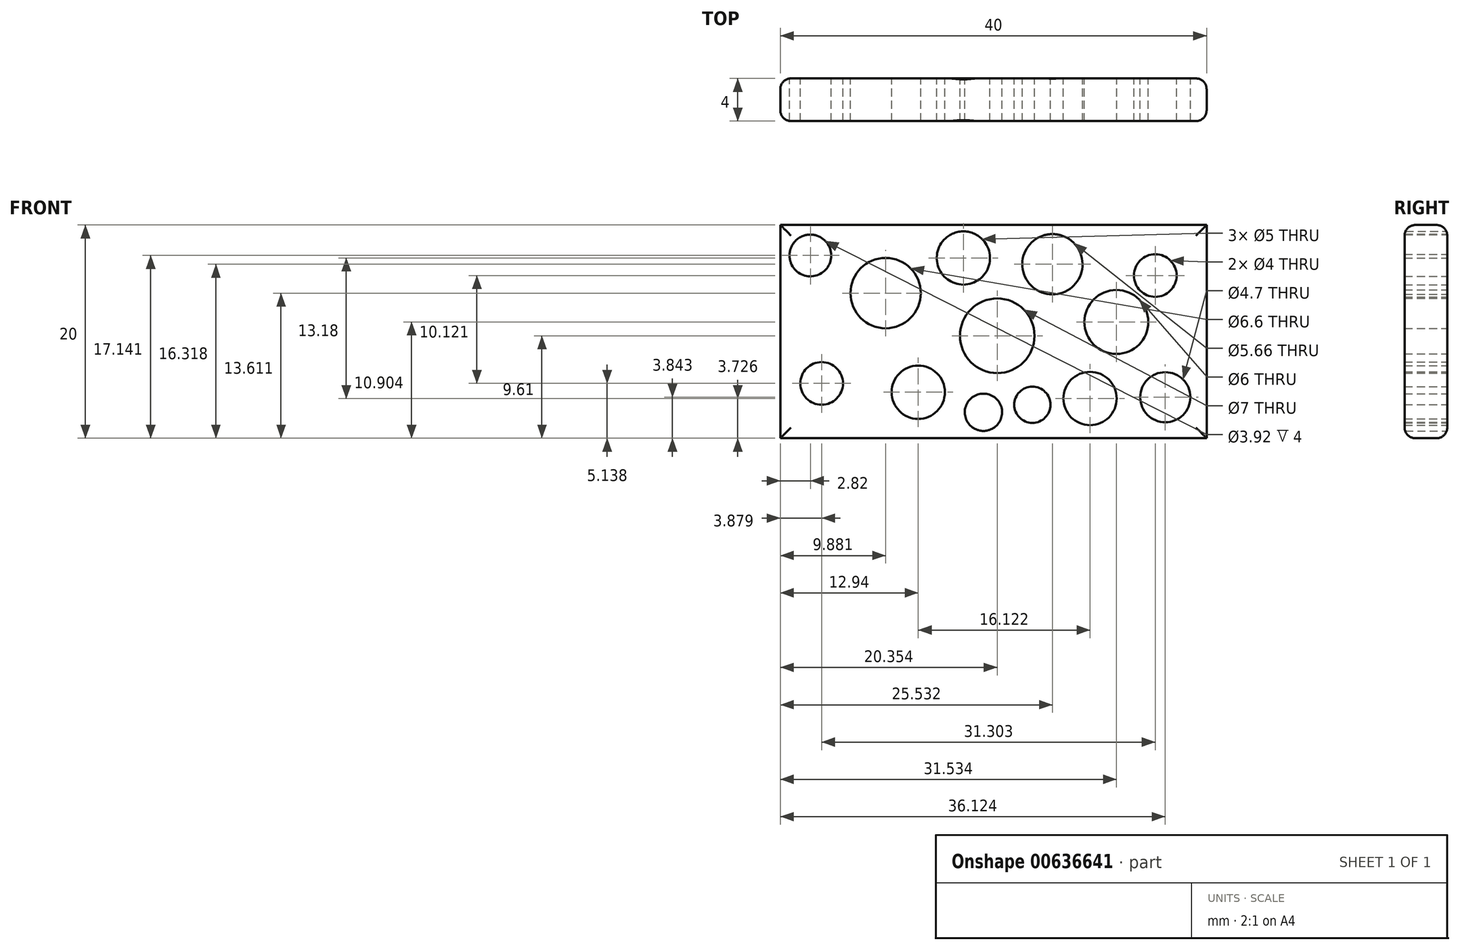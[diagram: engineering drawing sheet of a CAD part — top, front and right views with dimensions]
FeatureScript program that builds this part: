
annotation { "Feature Type Name" : "Feature", "Feature Type Description" : "" }
export const myFeature = defineFeature(function(context is Context, id is Id, definition is map)
    precondition{}
    {
        {
            var Q0;
            Q0=qCreatedBy(makeId("Front.planeOp"),FACE);
            var sketch = newSketch(context, id + "F0", { "sketchPlane" : qUnion([Q0])});
            skLineSegment(sketch, "E0", {"start": v(0, 0) * mm, "end": v(0, 20) * mm});
            skLineSegment(sketch, "E1", {"start": v(0, 20) * mm, "end": v(40, 20) * mm});
            skLineSegment(sketch, "E2", {"start": v(40, 20) * mm, "end": v(40, 0) * mm});
            skLineSegment(sketch, "E3", {"start": v(40, 0) * mm, "end": v(0, 0) * mm});
            skCircle(sketch, "E4", {"center": v(12.94, 4.31) * mm, "radius": 2.5 * mm});
            skCircle(sketch, "E5", {"center": v(20.35, 9.6) * mm, "radius": 3.5 * mm});
            skCircle(sketch, "E6", {"center": v(29.06, 3.73) * mm, "radius": 2.5 * mm});
            skCircle(sketch, "E7", {"center": v(31.53, 10.9) * mm, "radius": 3 * mm});
            skCircle(sketch, "E8", {"center": v(25.53, 16.32) * mm, "radius": 2.83 * mm});
            skCircle(sketch, "E9", {"center": v(9.88, 13.61) * mm, "radius": 3.3 * mm});
            skCircle(sketch, "E10", {"center": v(3.88, 5.14) * mm, "radius": 2 * mm});
            skCircle(sketch, "E11", {"center": v(35.18, 15.26) * mm, "radius": 2 * mm});
            skCircle(sketch, "E12", {"center": v(36.12, 3.84) * mm, "radius": 2.35 * mm});
            skCircle(sketch, "E13", {"center": v(19.06, 2.43) * mm, "radius": 1.75 * mm});
            skCircle(sketch, "E14", {"center": v(23.65, 3.14) * mm, "radius": 1.7 * mm});
            skCircle(sketch, "E15", {"center": v(17.18, 16.9) * mm, "radius": 2.5 * mm});
            skCircle(sketch, "E16", {"center": v(2.82, 17.14) * mm, "radius": 1.96 * mm});
            skSolve(sketch);
        }
        {
            var Q0;
            Q0=makeQuery(id+"F0.imprint","IMPRINT",FACE,{"disambiguationData":[TD([[makeQuery(id+"F0.imprint","IMPRINT",EDGE,{"derivedFrom":sQuery(id+"F0.wireOp",EDGE,"E0")}),-1.0]])]});
            extrude(context, id + "F1", {"entities" : qUnion([Q0]), "depth" : 4 * mm, "offsetDistance" : 25 * mm});
        }
        {
            var Q0;
            Q0=makeQuery(id+"F1.opExtrude","CAP_EDGE",EDGE,{"disambiguationData":[OSD([sQuery(id+"F0.wireOp",EDGE,"E0")])],"isStart":false});
            var Q1;
            Q1=makeQuery(id+"F1.opExtrude","CAP_EDGE",EDGE,{"disambiguationData":[OSD([sQuery(id+"F0.wireOp",EDGE,"E1")])],"isStart":false});
            var Q2;
            Q2=makeQuery(id+"F1.opExtrude","CAP_EDGE",EDGE,{"disambiguationData":[OSD([sQuery(id+"F0.wireOp",EDGE,"E2")])],"isStart":false});
            var Q3;
            Q3=makeQuery(id+"F1.opExtrude","CAP_EDGE",EDGE,{"disambiguationData":[OSD([sQuery(id+"F0.wireOp",EDGE,"E3")])],"isStart":false});
            var Q4;
            Q4=makeQuery(id+"F1.opExtrude","CAP_EDGE",EDGE,{"disambiguationData":[OSD([sQuery(id+"F0.wireOp",EDGE,"E0")])],"isStart":true});
            var Q5;
            Q5=makeQuery(id+"F1.opExtrude","CAP_EDGE",EDGE,{"disambiguationData":[OSD([sQuery(id+"F0.wireOp",EDGE,"E1")])],"isStart":true});
            var Q6;
            Q6=makeQuery(id+"F1.opExtrude","CAP_EDGE",EDGE,{"disambiguationData":[OSD([sQuery(id+"F0.wireOp",EDGE,"E2")])],"isStart":true});
            var Q7;
            Q7=makeQuery(id+"F1.opExtrude","CAP_EDGE",EDGE,{"disambiguationData":[OSD([sQuery(id+"F0.wireOp",EDGE,"E3")])],"isStart":true});
            fillet(context, id + "F2", {"entities" : qUnion([Q0, Q1, Q2, Q3, Q4, Q5, Q6, Q7]), "radius" : 1 * mm, "tangentPropagation" : true, "allowEdgeOverflow" : false});
        }
    });
